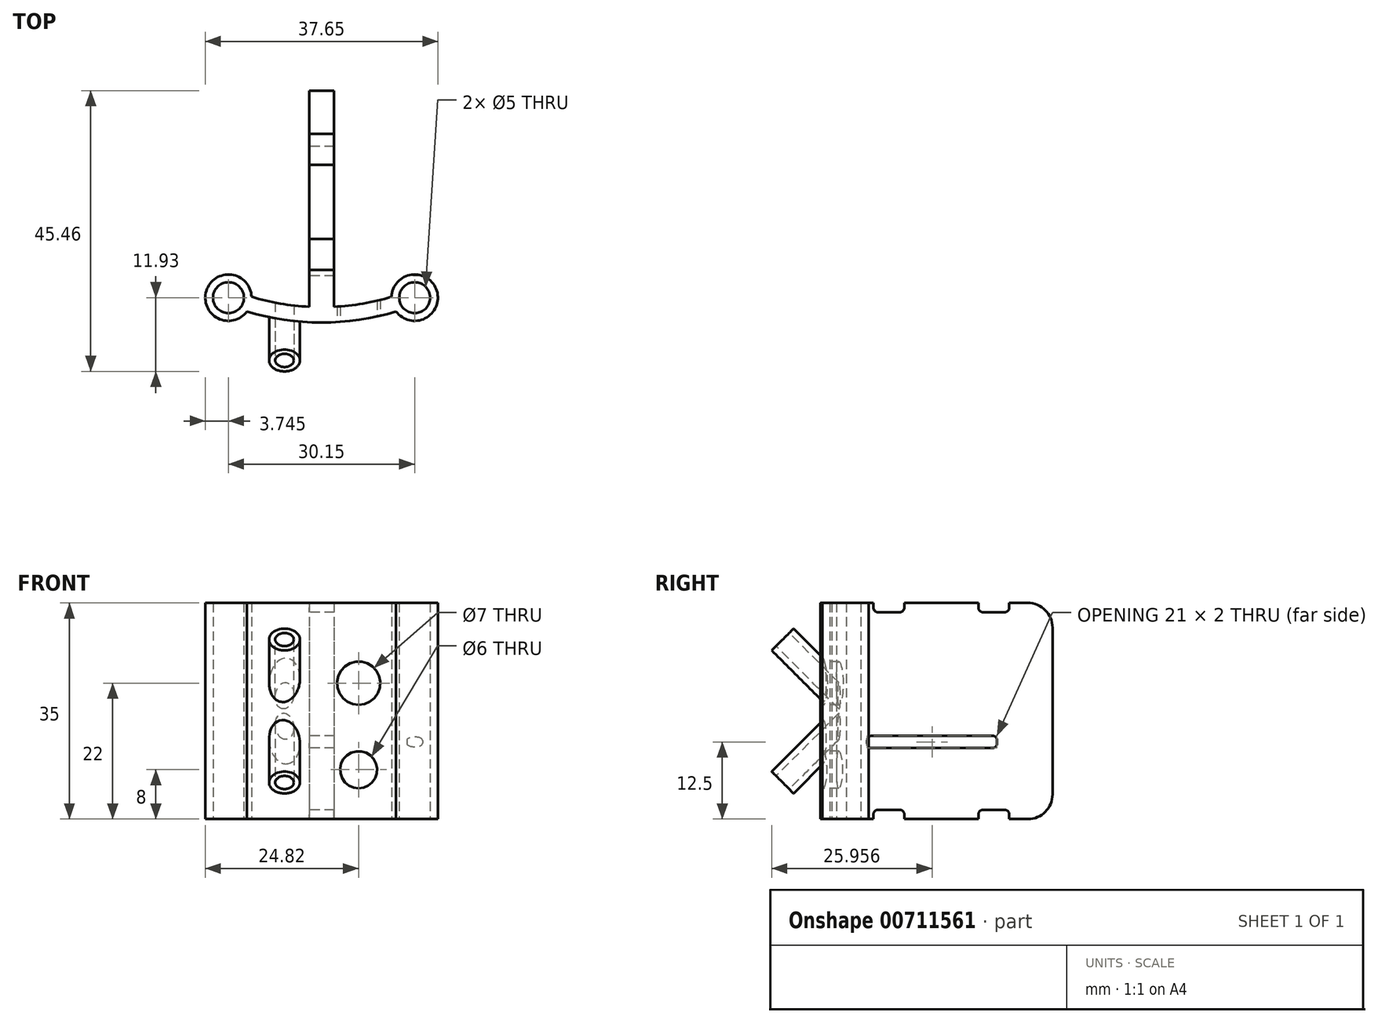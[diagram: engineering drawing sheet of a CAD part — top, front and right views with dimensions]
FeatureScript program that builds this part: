
annotation { "Feature Type Name" : "Feature", "Feature Type Description" : "" }
export const myFeature = defineFeature(function(context is Context, id is Id, definition is map)
    precondition{}
    {
        {
            var Q0;
            Q0=qCreatedBy(makeId("Front.planeOp"),FACE);
            var sketch = newSketch(context, id + "F0", { "sketchPlane" : qUnion([Q0])});
            skLineSegment(sketch, "E0.bottom", {"start": v(15.08, 17.5) * mm, "end": v(-15.07, 17.5) * mm});
            skLineSegment(sketch, "E0.top", {"start": v(15.07, -17.5) * mm, "end": v(-15.08, -17.5) * mm});
            skLineSegment(sketch, "E0.left", {"start": v(15.07, 17.5) * mm, "end": v(15.07, -17.5) * mm, "construction": true});
            skLineSegment(sketch, "E0.right", {"start": v(-15.07, 17.5) * mm, "end": v(-15.08, -17.5) * mm, "construction": true});
            skPoint(sketch, "E0.middle", {"position": v(0, 0) * mm});
            skSolve(sketch);
        }
        {
            var Q0;
            Q0=qCreatedBy(makeId("Top.planeOp"),FACE);
            var sketch = newSketch(context, id + "F1", { "sketchPlane" : qUnion([Q0])});
            skCircle(sketch, "E1", {"center": v(15.07, 0) * mm, "radius": 2.5 * mm});
            skCircle(sketch, "E2", {"center": v(-15.07, 0) * mm, "radius": 2.5 * mm});
            skCircle(sketch, "E3", {"center": v(-15.07, 0) * mm, "radius": 3.75 * mm});
            skCircle(sketch, "E4", {"center": v(15.07, 0) * mm, "radius": 3.75 * mm});
            skPoint(sketch, "E5.middle", {"position": v(0, 0) * mm});
            skArc(sketch, "E6", {"start": v(-12.07, -2.24) * mm, "mid": v(0, -4.03) * mm, "end": v(12.07, -2.24) * mm});
            skArc(sketch, "E7", {"start": v(-11.33, 0.15) * mm, "mid": v(0, -1.53) * mm, "end": v(11.34, 0.15) * mm});
            skLineSegment(sketch, "E8", {"start": v(2, -1.47) * mm, "end": v(2, 33.53) * mm});
            skLineSegment(sketch, "E9", {"start": v(-2, -1.47) * mm, "end": v(-2, 33.53) * mm});
            skLineSegment(sketch, "E10", {"start": v(-2, 33.53) * mm, "end": v(2, 33.53) * mm});
            skSolve(sketch);
        }
        {
            var Q0;
            Q0=makeQuery(id+"F1.imprint","IMPRINT",FACE,{"disambiguationData":[TD([[makeQuery(id+"F1.imprint","IMPRINT",EDGE,{"derivedFrom":sQuery(id+"F1.wireOp",EDGE,"E2")}),-1.0]])]});
            var Q1;
            Q1=makeQuery(id+"F1.imprint","IMPRINT",FACE,{"disambiguationData":[TD([[makeQuery(id+"F1.imprint","IMPRINT",EDGE,{"derivedFrom":sQuery(id+"F1.wireOp",EDGE,"E1")}),-1.0]])]});
            var Q2;
            {var subQ0=sQuery(id+"F1.wireOp",EDGE,"E6");Q2=makeQuery(id+"F1.imprint","IMPRINT",FACE,{"disambiguationData":[TD([[makeQuery(id+"F1.imprint","IMPRINT",EDGE,{"derivedFrom":subQ0}),1.0]])]});}
            var Q3;
            {var subQ0=sQuery(id+"F1.wireOp",EDGE,"E8");Q3=makeQuery(id+"F1.imprint","IMPRINT",FACE,{"disambiguationData":[TD([[makeQuery(id+"F1.imprint","IMPRINT",EDGE,{"derivedFrom":subQ0}),1.0]])]});}
            extrude(context, id + "F2", {"entities" : qUnion([Q0, Q1, Q2, Q3]), "depth" : 17.5 * mm, "offsetDistance" : 25 * mm, "hasSecondDirection" : true, "secondDirectionOppositeDirection" : true, "secondDirectionDepth" : 17.5 * mm});
        }
        {
            var Q0;
            Q0=makeQuery(id+"F2.opExtrude","CAP_EDGE",EDGE,{"disambiguationData":[OSD([sQuery(id+"F1.wireOp",EDGE,"E10")])],"isStart":false});
            var Q1;
            Q1=makeQuery(id+"F2.opExtrude","CAP_EDGE",EDGE,{"disambiguationData":[OSD([sQuery(id+"F1.wireOp",EDGE,"E10")])],"isStart":true});
            fillet(context, id + "F3", {"entities" : qUnion([Q0, Q1]), "radius" : 4 * mm, "tangentPropagation" : true, "allowEdgeOverflow" : false});
        }
        {
            var Q0;
            Q0=makeQuery(id+"F2.opExtrude","SWEPT_FACE",FACE,{"disambiguationData":[OSD([sQuery(id+"F1.wireOp",EDGE,"E9")])]});
            var sketch = newSketch(context, id + "F4", { "sketchPlane" : qUnion([Q0])});
            skLineSegment(sketch, "E11.bottom", {"start": v(-24.53, 11) * mm, "end": v(-3.53, 11) * mm});
            skLineSegment(sketch, "E12.bottom", {"start": v(-23.78, 11) * mm, "end": v(-4.28, 11) * mm});
            skLineSegment(sketch, "E12.top", {"start": v(-23.78, 13) * mm, "end": v(-4.28, 13) * mm});
            skLineSegment(sketch, "E12.left", {"start": v(-24.53, 11.75) * mm, "end": v(-24.53, 12.25) * mm});
            skLineSegment(sketch, "E12.right", {"start": v(-3.53, 11.75) * mm, "end": v(-3.53, 12.25) * mm});
            skPoint(sketch, "E11.top.end.orphan", {"position": v(-6.53, 0) * mm});
            skPoint(sketch, "E13.visualSharp", {"position": v(-24.53, 13) * mm});
            skArc(sketch, "E13.filletArc", {"start": v(-23.78, 13) * mm, "mid": v(-24.3, 12.78) * mm, "end": v(-24.53, 12.25) * mm});
            skPoint(sketch, "E14.visualSharp", {"position": v(-24.53, 11) * mm});
            skArc(sketch, "E14.filletArc", {"start": v(-24.53, 11.75) * mm, "mid": v(-24.3, 11.22) * mm, "end": v(-23.78, 11) * mm});
            skPoint(sketch, "E15.visualSharp", {"position": v(-3.53, 13) * mm});
            skArc(sketch, "E15.filletArc", {"start": v(-3.53, 12.25) * mm, "mid": v(-3.75, 12.78) * mm, "end": v(-4.28, 13) * mm});
            skPoint(sketch, "E16.visualSharp", {"position": v(-3.53, 11) * mm});
            skArc(sketch, "E16.filletArc", {"start": v(-4.28, 11) * mm, "mid": v(-3.75, 11.22) * mm, "end": v(-3.53, 11.75) * mm});
            skLineSegment(sketch, "E17.bottom", {"start": v(-26.53, -17.5) * mm, "end": v(-21.53, -17.5) * mm});
            skLineSegment(sketch, "E17.top", {"start": v(-25.78, -16) * mm, "end": v(-22.28, -16) * mm});
            skLineSegment(sketch, "E17.left", {"start": v(-26.53, -17.5) * mm, "end": v(-26.53, -16.75) * mm});
            skLineSegment(sketch, "E17.right", {"start": v(-21.53, -17.5) * mm, "end": v(-21.53, -16.75) * mm});
            skLineSegment(sketch, "E18.bottom", {"start": v(-9.53, -17.5) * mm, "end": v(-4.53, -17.5) * mm});
            skLineSegment(sketch, "E18.top", {"start": v(-8.78, -16) * mm, "end": v(-5.28, -16) * mm});
            skLineSegment(sketch, "E18.left", {"start": v(-9.53, -17.5) * mm, "end": v(-9.53, -16.75) * mm});
            skLineSegment(sketch, "E18.right", {"start": v(-4.53, -17.5) * mm, "end": v(-4.53, -16.75) * mm});
            skPoint(sketch, "E19.visualSharp", {"position": v(-26.53, -16) * mm});
            skArc(sketch, "E19.filletArc", {"start": v(-25.78, -16) * mm, "mid": v(-26.3, -16.22) * mm, "end": v(-26.53, -16.75) * mm});
            skPoint(sketch, "E20.visualSharp", {"position": v(-21.53, -16) * mm});
            skArc(sketch, "E20.filletArc", {"start": v(-21.53, -16.75) * mm, "mid": v(-21.75, -16.22) * mm, "end": v(-22.28, -16) * mm});
            skPoint(sketch, "E21.visualSharp", {"position": v(-9.53, -16) * mm});
            skArc(sketch, "E21.filletArc", {"start": v(-8.78, -16) * mm, "mid": v(-9.3, -16.22) * mm, "end": v(-9.53, -16.75) * mm});
            skPoint(sketch, "E22.visualSharp", {"position": v(-4.53, -16) * mm});
            skArc(sketch, "E22.filletArc", {"start": v(-4.53, -16.75) * mm, "mid": v(-4.75, -16.22) * mm, "end": v(-5.28, -16) * mm});
            skLineSegment(sketch, "E23.MirrorCS", {"start": v(-25.78, 16) * mm, "end": v(-22.28, 16) * mm});
            skPoint(sketch, "E24.MirrorP", {"position": v(-26.53, 16) * mm});
            skLineSegment(sketch, "E25.MirrorCS", {"start": v(-26.53, 17.5) * mm, "end": v(-26.53, 16.75) * mm});
            skArc(sketch, "E26.MirrorCS", {"start": v(-25.78, 16) * mm, "mid": v(-26.3, 16.22) * mm, "end": v(-26.53, 16.75) * mm});
            skLineSegment(sketch, "E27.MirrorCS", {"start": v(-26.53, 17.5) * mm, "end": v(-21.53, 17.5) * mm});
            skLineSegment(sketch, "E28.MirrorCS", {"start": v(-21.53, 17.5) * mm, "end": v(-21.53, 16.75) * mm});
            skArc(sketch, "E29.MirrorCS", {"start": v(-21.53, 16.75) * mm, "mid": v(-21.75, 16.22) * mm, "end": v(-22.28, 16) * mm});
            skLineSegment(sketch, "E30.MirrorCS", {"start": v(-4.53, 17.5) * mm, "end": v(-4.53, 16.75) * mm});
            skArc(sketch, "E31.MirrorCS", {"start": v(-4.53, 16.75) * mm, "mid": v(-4.75, 16.22) * mm, "end": v(-5.28, 16) * mm});
            skLineSegment(sketch, "E32.MirrorCS", {"start": v(-8.78, 16) * mm, "end": v(-5.28, 16) * mm});
            skArc(sketch, "E33.MirrorCS", {"start": v(-8.78, 16) * mm, "mid": v(-9.3, 16.22) * mm, "end": v(-9.53, 16.75) * mm});
            skLineSegment(sketch, "E34.MirrorCS", {"start": v(-9.53, 17.5) * mm, "end": v(-9.53, 16.75) * mm});
            skLineSegment(sketch, "E35.MirrorCS", {"start": v(-9.53, 17.5) * mm, "end": v(-4.53, 17.5) * mm});
            skLineSegment(sketch, "E36.bottom", {"start": v(-23.78, -4) * mm, "end": v(-4.28, -4) * mm});
            skLineSegment(sketch, "E36.top", {"start": v(-23.78, -6) * mm, "end": v(-4.28, -6) * mm});
            skLineSegment(sketch, "E36.left", {"start": v(-24.53, -4.75) * mm, "end": v(-24.53, -5.25) * mm});
            skLineSegment(sketch, "E36.right", {"start": v(-3.53, -4.75) * mm, "end": v(-3.53, -5.25) * mm});
            skPoint(sketch, "E37.visualSharp", {"position": v(-24.53, -4) * mm});
            skArc(sketch, "E37.filletArc", {"start": v(-23.78, -4) * mm, "mid": v(-24.3, -4.22) * mm, "end": v(-24.53, -4.75) * mm});
            skPoint(sketch, "E38.visualSharp", {"position": v(-24.53, -6) * mm});
            skArc(sketch, "E38.filletArc", {"start": v(-24.53, -5.25) * mm, "mid": v(-24.3, -5.78) * mm, "end": v(-23.78, -6) * mm});
            skPoint(sketch, "E39.visualSharp", {"position": v(-3.53, -6) * mm});
            skArc(sketch, "E39.filletArc", {"start": v(-4.28, -6) * mm, "mid": v(-3.75, -5.78) * mm, "end": v(-3.53, -5.25) * mm});
            skPoint(sketch, "E40.visualSharp", {"position": v(-3.53, -4) * mm});
            skArc(sketch, "E40.filletArc", {"start": v(-3.53, -4.75) * mm, "mid": v(-3.75, -4.22) * mm, "end": v(-4.28, -4) * mm});
            skSolve(sketch);
        }
        {
            var Q0;
            Q0=makeQuery(id+"F4.imprint","IMPRINT",FACE,{"disambiguationData":[TD([[makeQuery(id+"F4.imprint","IMPRINT",EDGE,{"derivedFrom":sQuery(id+"F4.wireOp",EDGE,"E12.bottom")}),1.0]])]});
            var Q1;
            {var subQ3=sQuery(id+"F4.wireOp",EDGE,"43c905df-29e5-4ef1-9885-413a96893caf0.MirrorCS");Q1=makeQuery(id+"F4.imprint","IMPRINT",FACE,{"disambiguationData":[TD([[makeQuery(id+"F4.imprint","IMPRINT",EDGE,{"derivedFrom":subQ3}),-1.0]])]});}
            var Q2;
            Q2=makeQuery(id+"F4.imprint","IMPRINT",FACE,{"disambiguationData":[TD([[makeQuery(id+"F4.imprint","IMPRINT",EDGE,{"derivedFrom":sQuery(id+"F4.wireOp",EDGE,"E36.bottom")}),-1.0]])]});
            extrude(context, id + "F5", {"entities" : qUnion([Q0, Q1, Q2]), "operationType" : NewBodyOperationType.REMOVE, "oppositeDirection" : true, "depth" : 25 * mm, "offsetDistance" : 25 * mm});
        }
        {
            var Q0;
            Q0=qCreatedBy(makeId("Front.planeOp"),FACE);
            cPlane(context, id + "F6", {"entities" : qUnion([Q0]), "cplaneType" : CPlaneType.OFFSET, "offset" : 5 * mm, "width" : 150 * mm, "height" : 150 * mm});
        }
        {
            var Q0;
            Q0=qCreatedBy(id+"F6.planeOp",FACE);
            var sketch = newSketch(context, id + "F7", { "sketchPlane" : qUnion([Q0])});
            skCircle(sketch, "E41", {"center": v(6, -9.5) * mm, "radius": 3 * mm});
            skCircle(sketch, "E42", {"center": v(6, 4.5) * mm, "radius": 3.5 * mm});
            skSolve(sketch);
        }
        {
            var Q0;
            Q0 = qSketchRegion(id + "F7", true);
            var Q1;
            Q1 = qSketchRegion(id + "F2RGtLKUElXccsK_1", true);
            extrude(context, id + "F8", {"entities" : qUnion([Q0, Q1]), "operationType" : NewBodyOperationType.REMOVE, "oppositeDirection" : true, "depth" : 25 * mm, "offsetDistance" : 25 * mm});
        }
        {
            var Q0;
            Q0=sQuery(id+"F0.wireOp",EDGE,"E0.top");
            cPlane(context, id + "F9", {"entities" : qUnion([Q0]), "cplaneType" : CPlaneType.LINE_ANGLE, "offset" : 10 * mm, "angle" : 45 * degree, "oppositeDirection" : true, "width" : 150 * mm, "height" : 150 * mm});
        }
        {
            var Q0;
            Q0=qCreatedBy(id+"F9.planeOp",FACE);
            var sketch = newSketch(context, id + "F10", { "sketchPlane" : qUnion([Q0])});
            skCircle(sketch, "E43", {"center": v(-6, -1) * mm, "radius": 2.5 * mm});
            skCircle(sketch, "E44", {"center": v(-6, -1) * mm, "radius": 1.5 * mm});
            skSolve(sketch);
        }
        {
            var Q0;
            Q0 = qSketchRegion(id + "F10", true);
            var Q1;
            Q1=makeQuery(id+"F2.opExtrude","SWEPT_FACE",FACE,{"disambiguationData":[OSD([sQuery(id+"F1.wireOp",EDGE,"E6")])]});
            extrude(context, id + "F11", {"entities" : qUnion([Q0]), "operationType" : NewBodyOperationType.ADD, "endBound" : BoundingType.UP_TO_SURFACE, "oppositeDirection" : true, "depth" : 5.4 * mm, "endBoundEntityFace" : qUnion([Q1]), "offsetDistance" : 25 * mm, "hasSecondDirection" : true, "secondDirectionOppositeDirection" : false, "secondDirectionDepth" : 3 * mm});
        }
        {
            var Q0;
            Q0=makeQuery(id+"F10.imprint","IMPRINT",FACE,{"disambiguationData":[TD([[makeQuery(id+"F10.imprint","IMPRINT",EDGE,{"derivedFrom":sQuery(id+"F10.wireOp",EDGE,"E44")}),1.0]])]});
            extrude(context, id + "F12", {"entities" : qUnion([Q0]), "operationType" : NewBodyOperationType.REMOVE, "oppositeDirection" : true, "depth" : 25 * mm, "offsetDistance" : 25 * mm});
        }
        {
            var Q0;
            Q0=sQuery(id+"F0.wireOp",EDGE,"E0.bottom");
            cPlane(context, id + "F13", {"entities" : qUnion([Q0]), "cplaneType" : CPlaneType.LINE_ANGLE, "offset" : 25 * mm, "angle" : 45 * degree, "width" : 150 * mm, "height" : 150 * mm});
        }
        {
            var Q0;
            Q0=qCreatedBy(id+"F13.planeOp",FACE);
            var sketch = newSketch(context, id + "F14", { "sketchPlane" : qUnion([Q0])});
            skCircle(sketch, "E45", {"center": v(-6, 1) * mm, "radius": 2.5 * mm});
            skCircle(sketch, "E46", {"center": v(-6, 1) * mm, "radius": 1.5 * mm});
            skSolve(sketch);
        }
        {
            var Q0;
            Q0=makeQuery(id+"F14.imprint","IMPRINT",FACE,{"disambiguationData":[TD([[makeQuery(id+"F14.imprint","IMPRINT",EDGE,{"derivedFrom":sQuery(id+"F14.wireOp",EDGE,"E45")}),1.0]])]});
            var Q1;
            {var subQ1=sQuery(id+"F1.wireOp",EDGE,"E3");var subQ6=sQuery(id+"F1.wireOp",EDGE,"E6");Q1=makeQuery(id+"F11.boolean.opBoolean","SPLIT",FACE,{"disambiguationData":[TD([makeQuery(id+"F2.opExtrude","SWEPT_FACE",FACE,{"disambiguationData":[OSD([subQ1])]})])],"derivedFrom":makeQuery(id+"F2.opExtrude","SWEPT_FACE",FACE,{"disambiguationData":[OSD([subQ6])]})});}
            extrude(context, id + "F15", {"entities" : qUnion([Q0]), "operationType" : NewBodyOperationType.ADD, "endBound" : BoundingType.UP_TO_SURFACE, "oppositeDirection" : true, "depth" : 25 * mm, "endBoundEntityFace" : qUnion([Q1]), "offsetDistance" : 25 * mm, "hasSecondDirection" : true, "secondDirectionOppositeDirection" : false, "secondDirectionDepth" : 3 * mm});
        }
        {
            var Q0;
            Q0=makeQuery(id+"F14.imprint","IMPRINT",FACE,{"disambiguationData":[TD([[makeQuery(id+"F14.imprint","IMPRINT",EDGE,{"derivedFrom":sQuery(id+"F14.wireOp",EDGE,"E46")}),1.0]])]});
            extrude(context, id + "F16", {"entities" : qUnion([Q0]), "operationType" : NewBodyOperationType.REMOVE, "oppositeDirection" : true, "depth" : 25 * mm, "offsetDistance" : 25 * mm});
        }
        {
            var Q0;
            Q0=makeQuery(id+"F4.imprint","IMPRINT",FACE,{"disambiguationData":[TD([[makeQuery(id+"F4.imprint","IMPRINT",EDGE,{"derivedFrom":sQuery(id+"F4.wireOp",EDGE,"E17.bottom")}),-1.0]])]});
            var Q1;
            Q1=makeQuery(id+"F4.imprint","IMPRINT",FACE,{"disambiguationData":[TD([[makeQuery(id+"F4.imprint","IMPRINT",EDGE,{"derivedFrom":sQuery(id+"F4.wireOp",EDGE,"E18.bottom")}),-1.0]])]});
            var Q2;
            Q2=makeQuery(id+"F4.imprint","IMPRINT",FACE,{"disambiguationData":[TD([[makeQuery(id+"F4.imprint","IMPRINT",EDGE,{"derivedFrom":sQuery(id+"F4.wireOp",EDGE,"E23.MirrorCS")}),1.0]])]});
            var Q3;
            Q3=makeQuery(id+"F4.imprint","IMPRINT",FACE,{"disambiguationData":[TD([[makeQuery(id+"F4.imprint","IMPRINT",EDGE,{"derivedFrom":sQuery(id+"F4.wireOp",EDGE,"E30.MirrorCS")}),-1.0]])]});
            var Q4;
            Q4=sQuery(id+"F4.wireOp",EDGE,"E17.top");
            var Q5;
            Q5=sQuery(id+"F4.wireOp",EDGE,"E17.bottom");
            var Q6;
            Q6=sQuery(id+"F4.wireOp",EDGE,"E17.right");
            var Q7;
            Q7=sQuery(id+"F4.wireOp",EDGE,"E17.left");
            extrude(context, id + "F17", {"entities" : qUnion([Q0, Q1, Q2, Q3]), "operationType" : NewBodyOperationType.REMOVE, "surfaceEntities" : qUnion([Q4, Q5, Q6, Q7]), "oppositeDirection" : true, "depth" : 25 * mm, "offsetDistance" : 25 * mm});
        }
    });
